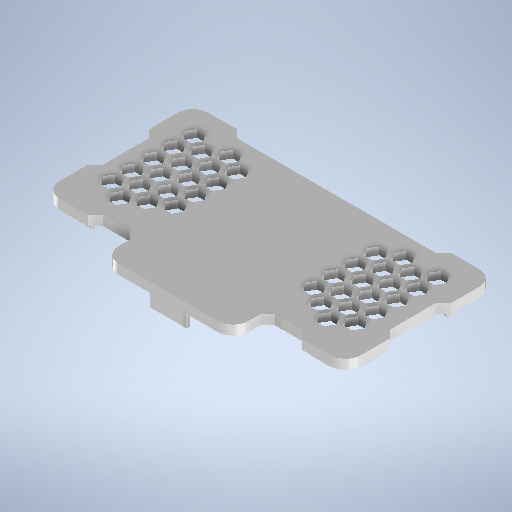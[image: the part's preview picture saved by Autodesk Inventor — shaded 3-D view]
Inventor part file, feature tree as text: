
AUTODESK INVENTOR PART (.ipt)
format: ipt  version: 2025.2 (Build 292293000, 293)  size: 1,759,744 bytes
history: native  units: mm
features: sketch x12, extrude x9, other x3, fillet x1, chamfer x1
ambient origin geometry x8: Origin, YZ Plane, XZ Plane, XY Plane, X Axis, Y Axis, Z Axis, Center Point
bodies: Body1 (feature_tree)
feature tree (26):
  other  "Bryła1"
  sketch  "Szkic1"
  extrude  "Wyciągnięcie proste1"  Depth=4.0mm
  extrude  "Wyciągnięcie proste4"  Depth=2.5mm TaperAngle=0.0deg
  extrude  "Wyciągnięcie proste6"  Depth=6.5mm
  extrude  "Wyciągnięcie proste7"  Depth=1.8mm
  other  "Płaszczyzna konstrukcyjna2"
  extrude  "Wyciągnięcie proste8"  Depth=6.5mm
  sketch  "Szkic10"
  sketch  "Szkic11"
  sketch  "Szkic12"
  sketch  "Szkic13"
  extrude  "Wyciągnięcie proste9"  Depth=1.8mm
  extrude  "Wyciągnięcie proste10"  Depth=3.0mm
  extrude  "Wyciągnięcie proste11"  Depth=1.6mm TaperAngle=0.0deg
  fillet  "Zaokrąglenie1"  Radius=3.5mm
  extrude  "Wyciągnięcie proste12"  Depth=9.38mm
  chamfer  "Faza4"  Distance=4.0mm
  sketch  "Szkic4"
  sketch  "Szkic5"
  sketch  "Szkic7"
  sketch  "Szkic14"
  sketch  "Szkic15"
  sketch  "Szkic16"
  sketch  "Szkic17"
  other  "Rzutuj krawędzie tnące1"
